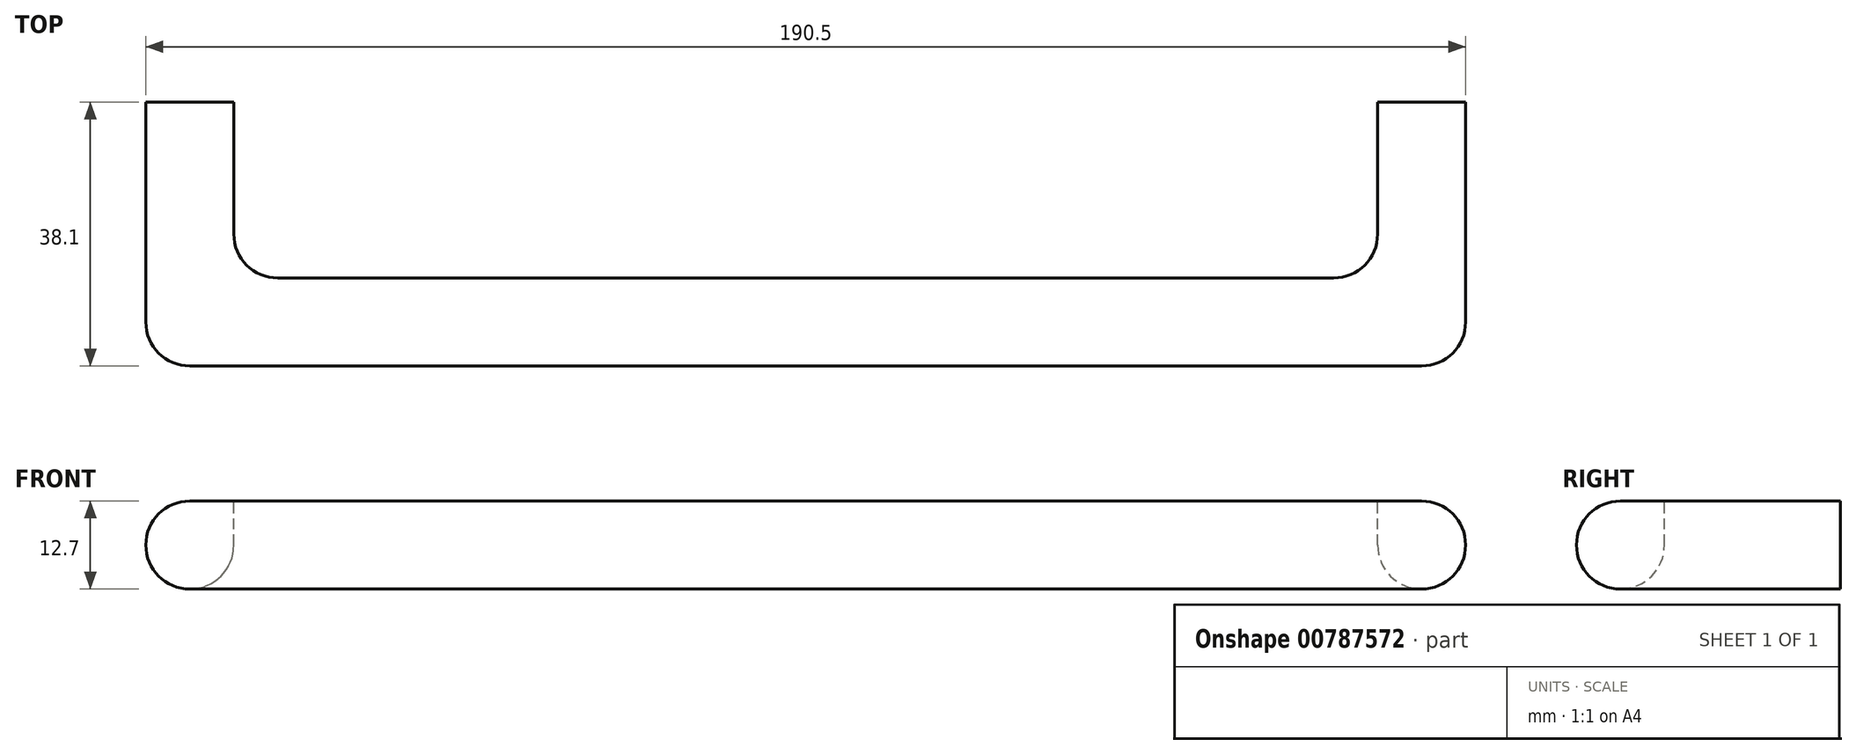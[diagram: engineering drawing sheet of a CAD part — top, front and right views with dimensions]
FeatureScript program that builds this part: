
annotation { "Feature Type Name" : "Feature", "Feature Type Description" : "" }
export const myFeature = defineFeature(function(context is Context, id is Id, definition is map)
    precondition{}
    {
        {
            var Q0;
            Q0=qCreatedBy(makeId("Front.planeOp"),FACE);
            var sketch = newSketch(context, id + "F0", { "sketchPlane" : qUnion([Q0])});
            skLineSegment(sketch, "E0.bottom", {"start": v(95.25, -6.35) * mm, "end": v(-95.25, -6.35) * mm});
            skLineSegment(sketch, "E0.top", {"start": v(95.25, 6.35) * mm, "end": v(-95.25, 6.35) * mm});
            skLineSegment(sketch, "E0.left", {"start": v(95.25, -6.35) * mm, "end": v(95.25, 6.35) * mm});
            skLineSegment(sketch, "E0.right", {"start": v(-95.25, -6.35) * mm, "end": v(-95.25, 6.35) * mm});
            skPoint(sketch, "E0.middle", {"position": v(0, 0) * mm});
            skSolve(sketch);
        }
        {
            var Q0;
            Q0 = qSketchRegion(id + "F0", true);
            extrude(context, id + "F1", {"entities" : qUnion([Q0]), "depth" : 38.1 * mm, "offsetDistance" : 25.4 * mm});
        }
        {
            var Q0;
            Q0=makeQuery(id+"F1.opExtrude","SWEPT_FACE",FACE,{"disambiguationData":[OSD([sQuery(id+"F0.wireOp",EDGE,"E0.top")])]});
            var sketch = newSketch(context, id + "F2", { "sketchPlane" : qUnion([Q0])});
            skLineSegment(sketch, "E1.bottom", {"start": v(-82.55, 0) * mm, "end": v(82.55, 0) * mm});
            skLineSegment(sketch, "E1.top", {"start": v(-82.55, -25.4) * mm, "end": v(82.55, -25.4) * mm});
            skLineSegment(sketch, "E1.left", {"start": v(-82.55, 0) * mm, "end": v(-82.55, -25.4) * mm});
            skLineSegment(sketch, "E1.right", {"start": v(82.55, 0) * mm, "end": v(82.55, -25.4) * mm});
            skSolve(sketch);
        }
        {
            var Q0;
            Q0 = qSketchRegion(id + "F2", true);
            extrude(context, id + "F3", {"entities" : qUnion([Q0]), "operationType" : NewBodyOperationType.REMOVE, "endBound" : BoundingType.THROUGH_ALL, "oppositeDirection" : true, "depth" : 25.4 * mm, "offsetDistance" : 25.4 * mm});
        }
        {
            var Q0;
            Q0=makeQuery(id+"F1.opExtrude","CAP_EDGE",EDGE,{"disambiguationData":[OSD([sQuery(id+"F0.wireOp",EDGE,"E0.right")])],"isStart":false});
            var Q1;
            Q1=makeQuery(id+"F3.boolean.opBoolean","COPY",EDGE,{"derivedFrom":makeQuery(id+"F3.opExtrude","SWEPT_EDGE",EDGE,{"disambiguationData":[OSD([sQuery(id+"F2.wireOp",EDGE,"E1.top"),sQuery(id+"F2.wireOp",EDGE,"E1.left")])]})});
            var Q2;
            Q2=makeQuery(id+"F1.opExtrude","CAP_EDGE",EDGE,{"disambiguationData":[OSD([sQuery(id+"F0.wireOp",EDGE,"E0.left")])],"isStart":false});
            var Q3;
            Q3=makeQuery(id+"F3.boolean.opBoolean","COPY",EDGE,{"derivedFrom":makeQuery(id+"F3.opExtrude","SWEPT_EDGE",EDGE,{"disambiguationData":[OSD([sQuery(id+"F2.wireOp",EDGE,"E1.top"),sQuery(id+"F2.wireOp",EDGE,"E1.right")])]})});
            var Q4;
            Q4=makeQuery(id+"F1.opExtrude","CAP_EDGE",EDGE,{"disambiguationData":[OSD([sQuery(id+"F0.wireOp",EDGE,"E0.top")])],"isStart":false});
            var Q5;
            Q5=makeQuery(id+"F3.boolean.opBoolean","COPY",EDGE,{"derivedFrom":makeQuery(id+"F3.opExtrude","CAP_EDGE",EDGE,{"disambiguationData":[OSD([sQuery(id+"F2.wireOp",EDGE,"E1.top")])],"isStart":true})});
            var Q6;
            Q6=makeQuery(id+"F1.opExtrude","CAP_EDGE",EDGE,{"disambiguationData":[OSD([sQuery(id+"F0.wireOp",EDGE,"E0.bottom")])],"isStart":false});
            var Q7;
            Q7=makeQuery(id+"F3.boolean.opBoolean","INTERSECT",EDGE,{"derivedFrom":[makeQuery(id+"F1.opExtrude","SWEPT_FACE",FACE,{"disambiguationData":[OSD([sQuery(id+"F0.wireOp",EDGE,"E0.bottom")])]}),makeQuery(id+"F3.opExtrude","SWEPT_FACE",FACE,{"disambiguationData":[OSD([sQuery(id+"F2.wireOp",EDGE,"E1.top")])]})]});
            var Q8;
            Q8=makeQuery(id+"F3.boolean.opBoolean","INTERSECT",EDGE,{"derivedFrom":[makeQuery(id+"F1.opExtrude","SWEPT_FACE",FACE,{"disambiguationData":[OSD([sQuery(id+"F0.wireOp",EDGE,"E0.bottom")])]}),makeQuery(id+"F3.opExtrude","SWEPT_FACE",FACE,{"disambiguationData":[OSD([sQuery(id+"F2.wireOp",EDGE,"E1.left")])]})]});
            var Q9;
            Q9=makeQuery(id+"F1.opExtrude","SWEPT_EDGE",EDGE,{"disambiguationData":[OSD([sQuery(id+"F0.wireOp",EDGE,"E0.bottom"),sQuery(id+"F0.wireOp",EDGE,"E0.right")])]});
            var Q10;
            Q10=makeQuery(id+"F3.boolean.opBoolean","INTERSECT",EDGE,{"derivedFrom":[makeQuery(id+"F1.opExtrude","SWEPT_FACE",FACE,{"disambiguationData":[OSD([sQuery(id+"F0.wireOp",EDGE,"E0.bottom")])]}),makeQuery(id+"F3.opExtrude","SWEPT_FACE",FACE,{"disambiguationData":[OSD([sQuery(id+"F2.wireOp",EDGE,"E1.right")])]})]});
            var Q11;
            Q11=makeQuery(id+"F1.opExtrude","SWEPT_EDGE",EDGE,{"disambiguationData":[OSD([sQuery(id+"F0.wireOp",EDGE,"E0.bottom"),sQuery(id+"F0.wireOp",EDGE,"E0.left")])]});
            var Q12;
            Q12=makeQuery(id+"F1.opExtrude","SWEPT_EDGE",EDGE,{"disambiguationData":[OSD([sQuery(id+"F0.wireOp",EDGE,"E0.top"),sQuery(id+"F0.wireOp",EDGE,"E0.left")])]});
            var Q13;
            Q13=makeQuery(id+"F3.boolean.opBoolean","COPY",EDGE,{"derivedFrom":makeQuery(id+"F3.opExtrude","CAP_EDGE",EDGE,{"disambiguationData":[OSD([sQuery(id+"F2.wireOp",EDGE,"E1.left")])],"isStart":true})});
            var Q14;
            Q14=makeQuery(id+"F1.opExtrude","SWEPT_EDGE",EDGE,{"disambiguationData":[OSD([sQuery(id+"F0.wireOp",EDGE,"E0.top"),sQuery(id+"F0.wireOp",EDGE,"E0.right")])]});
            var Q15;
            Q15=makeQuery(id+"F3.boolean.opBoolean","COPY",EDGE,{"derivedFrom":makeQuery(id+"F3.opExtrude","CAP_EDGE",EDGE,{"disambiguationData":[OSD([sQuery(id+"F2.wireOp",EDGE,"E1.right")])],"isStart":true})});
            fillet(context, id + "F4", {"entities" : qUnion([Q0, Q1, Q2, Q3, Q4, Q5, Q6, Q7, Q8, Q9, Q10, Q11, Q12, Q13, Q14, Q15]), "radius" : 6.35 * mm, "allowEdgeOverflow" : false});
        }
    });
